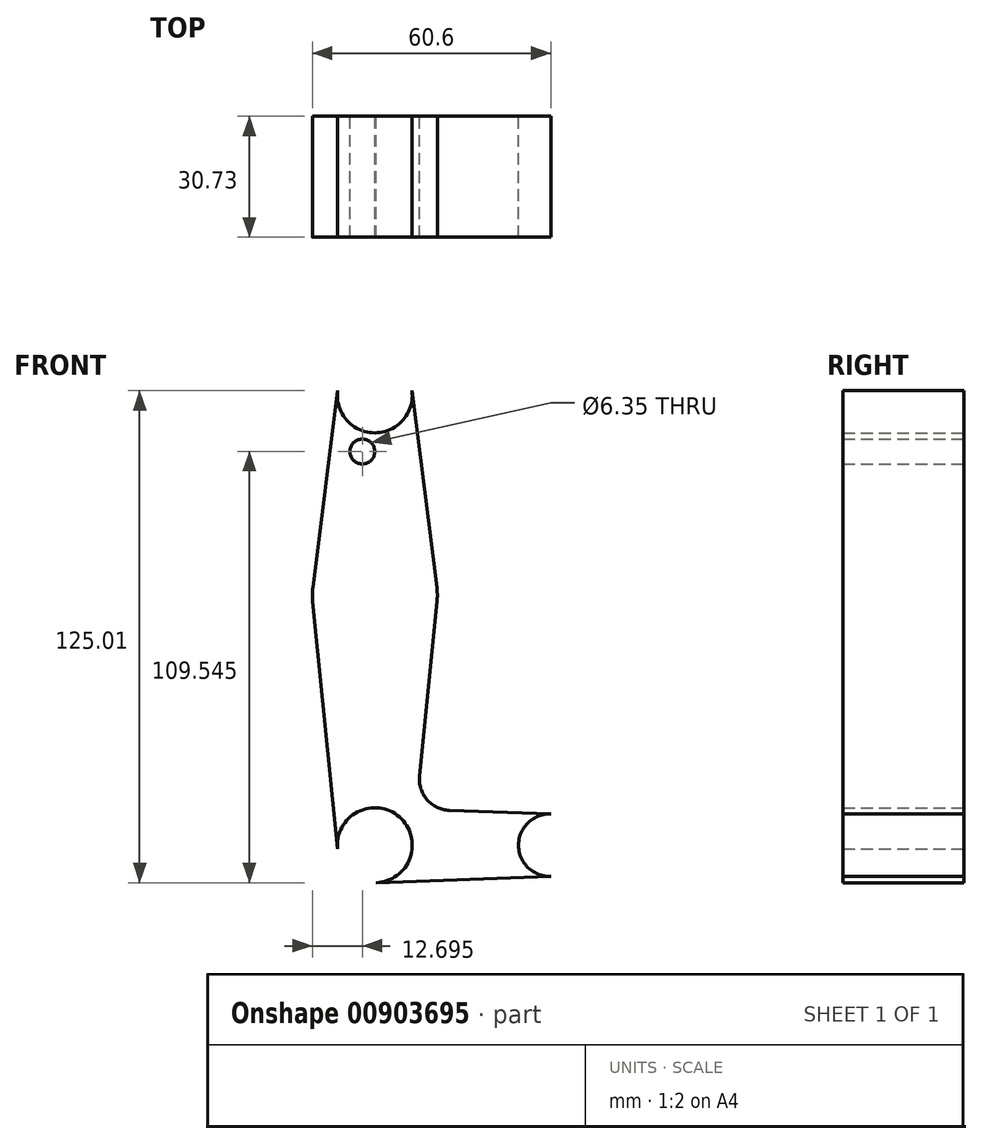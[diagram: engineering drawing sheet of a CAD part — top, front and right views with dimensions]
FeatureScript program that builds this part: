
annotation { "Feature Type Name" : "Feature", "Feature Type Description" : "" }
export const myFeature = defineFeature(function(context is Context, id is Id, definition is map)
    precondition{}
    {
        {
            var Q0;
            Q0=qCreatedBy(makeId("Front.planeOp"),FACE);
            var sketch = newSketch(context, id + "F0", { "sketchPlane" : qUnion([Q0])});
            skLineSegment(sketch, "E0", {"start": v(0, 0) * mm, "end": v(0, 114.3) * mm, "construction": true});
            skLineSegment(sketch, "E1", {"start": v(0, 0) * mm, "end": v(44.45, 0) * mm, "construction": true});
            skCircle(sketch, "E2", {"center": v(44.45, 0) * mm, "radius": 7.94 * mm});
            skCircle(sketch, "E3", {"center": v(0, 0) * mm, "radius": 9.53 * mm});
            skCircle(sketch, "E4", {"center": v(0, 63.5) * mm, "radius": 15.88 * mm});
            skCircle(sketch, "E5", {"center": v(0, 114.3) * mm, "radius": 9.53 * mm});
            skLineSegment(sketch, "E6", {"start": v(-15.8, 61.91) * mm, "end": v(-9.48, -0.95) * mm});
            skLineSegment(sketch, "E7", {"start": v(-15.75, 65.48) * mm, "end": v(-9.45, 115.5) * mm});
            skLineSegment(sketch, "E8", {"start": v(9.45, 115.5) * mm, "end": v(15.75, 65.48) * mm});
            skLineSegment(sketch, "E9", {"start": v(0.34, -9.52) * mm, "end": v(44.73, -7.93) * mm});
            skLineSegment(sketch, "E10", {"start": v(18.97, 8.85) * mm, "end": v(44.73, 7.93) * mm});
            skLineSegment(sketch, "E11", {"start": v(15.8, 61.91) * mm, "end": v(11.34, 17.6) * mm});
            skCircle(sketch, "E12", {"center": v(0, 114.3) * mm, "radius": 3.18 * mm});
            skCircle(sketch, "E13", {"center": v(0, 63.5) * mm, "radius": 3.18 * mm});
            skCircle(sketch, "E14", {"center": v(-3.18, 100.03) * mm, "radius": 3.18 * mm});
            skCircle(sketch, "E15", {"center": v(0, 0) * mm, "radius": 3.18 * mm});
            skCircle(sketch, "E16", {"center": v(44.45, 0) * mm, "radius": 3.18 * mm});
            skLineSegment(sketch, "E17", {"start": v(-3.18, 100.03) * mm, "end": v(0, 100.03) * mm, "construction": true});
            skArc(sketch, "E18.filletArc", {"start": v(11.34, 17.6) * mm, "mid": v(13.26, 11.57) * mm, "end": v(18.97, 8.85) * mm});
            skSolve(sketch);
        }
        {
            var Q0;
            Q0=makeQuery(id+"F0.imprint","IMPRINT",FACE,{"disambiguationData":[TD([[makeQuery(id+"F0.imprint","IMPRINT",EDGE,{"derivedFrom":sQuery(id+"F0.wireOp",EDGE,"E13")}),-1.0]])]});
            var Q1;
            Q1=makeQuery(id+"F0.imprint","IMPRINT",FACE,{"disambiguationData":[TD([[makeQuery(id+"F0.imprint","IMPRINT",EDGE,{"derivedFrom":sQuery(id+"F0.wireOp",EDGE,"E13")}),1.0]])]});
            var Q2;
            {var subQ0=sQuery(id+"F0.wireOp",EDGE,"E6");Q2=makeQuery(id+"F0.imprint","IMPRINT",FACE,{"disambiguationData":[TD([[makeQuery(id+"F0.imprint","IMPRINT",EDGE,{"derivedFrom":subQ0}),1.0]])]});}
            var Q3;
            {var subQ1=sQuery(id+"F0.wireOp",EDGE,"E7");Q3=makeQuery(id+"F0.imprint","IMPRINT",FACE,{"disambiguationData":[TD([[makeQuery(id+"F0.imprint","IMPRINT",EDGE,{"derivedFrom":subQ1}),-1.0]])]});}
            extrude(context, id + "F1", {"entities" : qUnion([Q0, Q1, Q2, Q3]), "depth" : 30.73 * mm, "offsetDistance" : 25.4 * mm});
        }
    });
